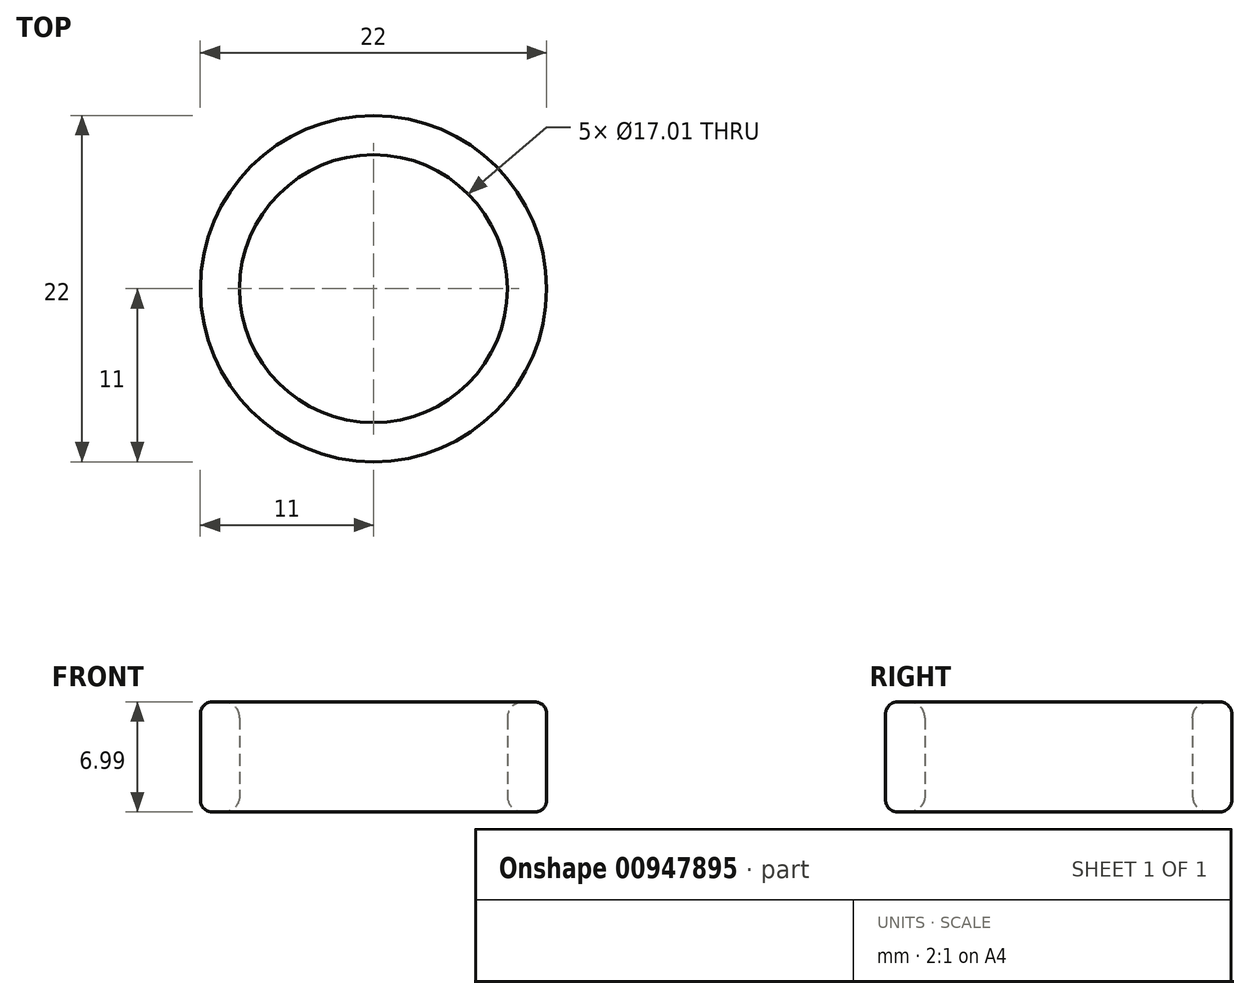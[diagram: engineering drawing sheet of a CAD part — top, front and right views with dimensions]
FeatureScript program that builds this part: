
annotation { "Feature Type Name" : "Feature", "Feature Type Description" : "" }
export const myFeature = defineFeature(function(context is Context, id is Id, definition is map)
    precondition{}
    {
        {
            var Q0;
            Q0=qCreatedBy(makeId("Top.planeOp"),FACE);
            var sketch = newSketch(context, id + "F0", { "sketchPlane" : qUnion([Q0])});
            skCircle(sketch, "E0", {"center": v(0, 0) * mm, "radius": 8.5 * mm});
            skCircle(sketch, "E1", {"center": v(0, 0) * mm, "radius": 11 * mm});
            skSolve(sketch);
        }
        {
            var Q0;
            Q0=makeQuery(id+"F0.imprint","IMPRINT",FACE,{"disambiguationData":[TD([[makeQuery(id+"F0.imprint","IMPRINT",EDGE,{"derivedFrom":sQuery(id+"F0.wireOp",EDGE,"E0")}),-1.0]])]});
            extrude(context, id + "F1", {"entities" : qUnion([Q0]), "depth" : 7 * mm, "offsetDistance" : 25 * mm});
        }
        {
            var Q0;
            Q0=makeQuery(id+"F1.opExtrude","CAP_EDGE",EDGE,{"disambiguationData":[OSD([sQuery(id+"F0.wireOp",EDGE,"E0")])],"isStart":false});
            var Q1;
            Q1=makeQuery(id+"F1.opExtrude","CAP_EDGE",EDGE,{"disambiguationData":[OSD([sQuery(id+"F0.wireOp",EDGE,"E0")])],"isStart":true});
            fillet(context, id + "F2", {"entities" : qUnion([Q0, Q1]), "radius" : 1 * mm, "tangentPropagation" : true, "allowEdgeOverflow" : false});
        }
        {
            var Q0;
            Q0=makeQuery(id+"F1.opExtrude","CAP_EDGE",EDGE,{"disambiguationData":[OSD([sQuery(id+"F0.wireOp",EDGE,"E1")])],"isStart":true});
            var Q1;
            Q1=makeQuery(id+"F1.opExtrude","CAP_EDGE",EDGE,{"disambiguationData":[OSD([sQuery(id+"F0.wireOp",EDGE,"E1")])],"isStart":false});
            fillet(context, id + "F3", {"entities" : qUnion([Q0, Q1]), "radius" : 0.75 * mm, "tangentPropagation" : true, "allowEdgeOverflow" : false});
        }
    });
